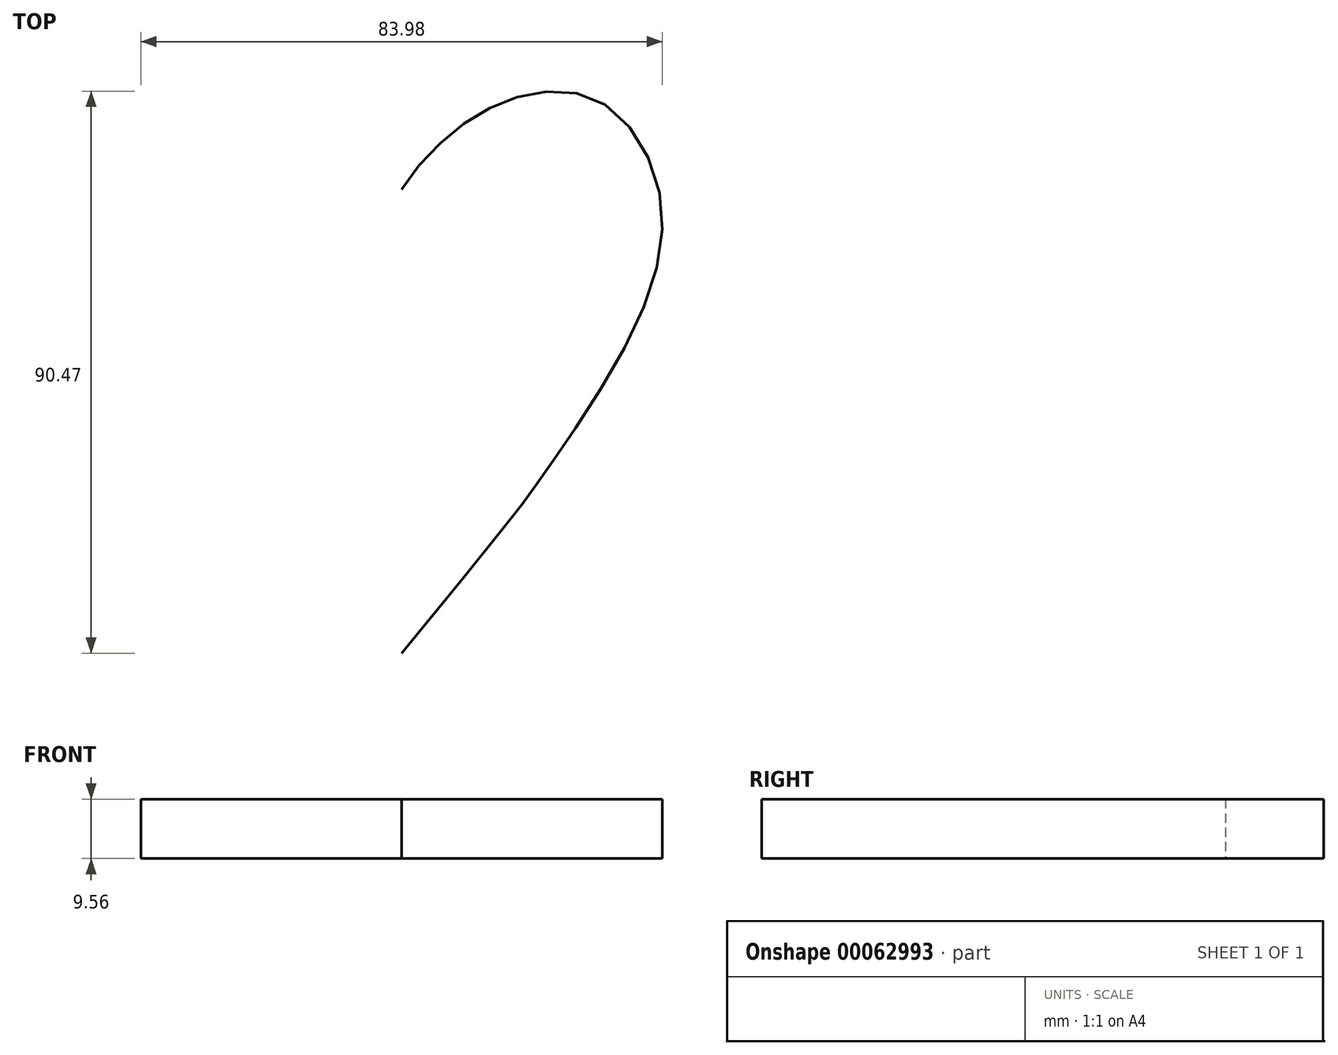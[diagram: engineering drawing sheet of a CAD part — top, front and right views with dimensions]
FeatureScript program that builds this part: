
annotation { "Feature Type Name" : "Feature", "Feature Type Description" : "" }
export const myFeature = defineFeature(function(context is Context, id is Id, definition is map)
    precondition{}
    {
        {
            var Q0;
            Q0=qCreatedBy(makeId("Top.planeOp"),FACE);
            var sketch = newSketch(context, id + "F0", { "sketchPlane" : qUnion([Q0])});
            skLineSegment(sketch, "E0", {"start": v(0, 27.92) * mm, "end": v(0, -46.73) * mm});
            skFitSpline(sketch, "E1", {"points": [v(0, 27.92) * mm, v(8.88, 37.64) * mm, v(20.2, 43.24) * mm, v(32.81, 41.53) * mm, v(41.63, 26.9) * mm, v(37.2, 5.06) * mm, v(23, -17.8) * mm, v(0, -46.73) * mm], "startDerivative": vector(56.25, 90.93) * mm, "endDerivative": vector(-288.27, -352.09) * mm});
            skFitSpline(sketch, "E2.MirrorCS", {"points": [v(0, 27.92) * mm, v(-8.88, 37.64) * mm, v(-20.2, 43.24) * mm, v(-32.81, 41.53) * mm, v(-41.63, 26.9) * mm, v(-37.2, 5.06) * mm, v(-23, -17.8) * mm, v(0, -46.73) * mm], "startDerivative": vector(-56.25, 90.93) * mm, "endDerivative": vector(288.27, -352.09) * mm});
            skSolve(sketch);
        }
        {
            var Q0;
            Q0=makeQuery(id+"F0.imprint","IMPRINT",FACE,{"disambiguationData":[TD([[makeQuery(id+"F0.imprint","IMPRINT",EDGE,{"derivedFrom":sQuery(id+"F0.wireOp",EDGE,"E0")}),1.0]])]});
            var Q1;
            Q1=makeQuery(id+"F0.imprint","IMPRINT",FACE,{"disambiguationData":[TD([[makeQuery(id+"F0.imprint","IMPRINT",EDGE,{"derivedFrom":sQuery(id+"F0.wireOp",EDGE,"E0")}),-1.0]])]});
            extrude(context, id + "F1", {"entities" : qUnion([Q0, Q1]), "depth" : 9.56 * mm});
        }
    });
